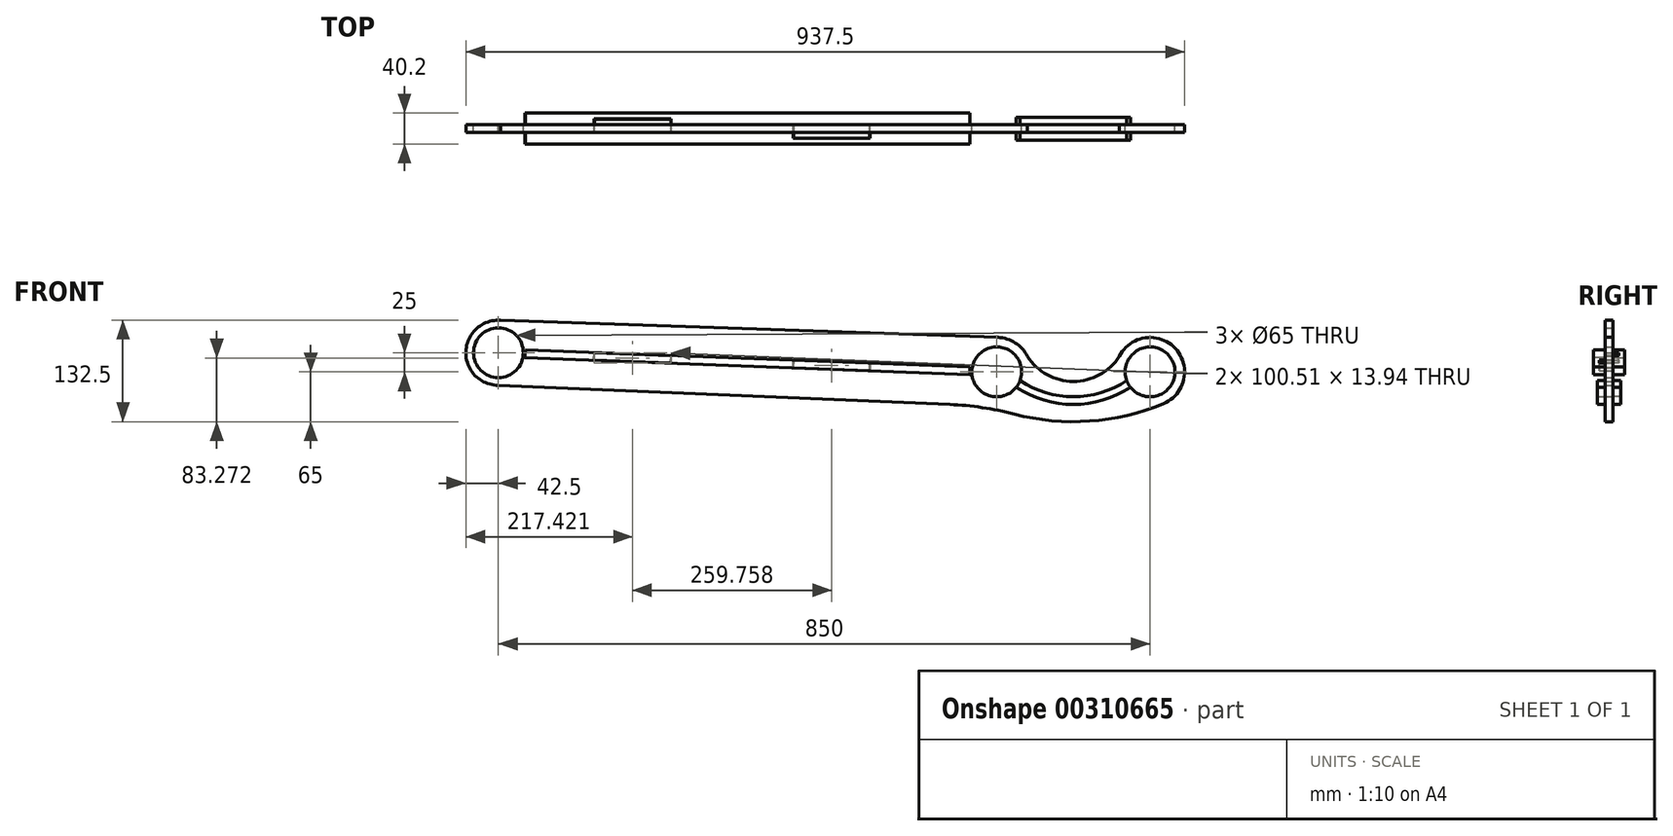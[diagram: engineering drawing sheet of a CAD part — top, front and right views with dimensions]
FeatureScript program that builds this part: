
annotation { "Feature Type Name" : "Feature", "Feature Type Description" : "" }
export const myFeature = defineFeature(function(context is Context, id is Id, definition is map)
    precondition{}
    {
        {
            var Q0;
            Q0=qCreatedBy(makeId("Front.planeOp"),FACE);
            var sketch = newSketch(context, id + "F0", { "sketchPlane" : qUnion([Q0])});
            skCircle(sketch, "E0", {"center": v(0, 0) * mm, "radius": 32.5 * mm});
            skCircle(sketch, "E1", {"center": v(0, 0) * mm, "radius": 42.5 * mm});
            skCircle(sketch, "E2", {"center": v(750, 0) * mm, "radius": 35 * mm, "construction": true});
            skArc(sketch, "E3", {"start": v(690.14, -4.65) * mm, "mid": v(674.21, 12.93) * mm, "end": v(651.55, 19.97) * mm});
            skCircle(sketch, "E4", {"center": v(850, -25) * mm, "radius": 45 * mm});
            skArc(sketch, "E5", {"start": v(687.42, 0) * mm, "mid": v(750, -37.5) * mm, "end": v(812.58, 0) * mm});
            skLineSegment(sketch, "E6", {"start": v(0, 42.5) * mm, "end": v(651.55, 19.97) * mm});
            skLineSegment(sketch, "E7", {"start": v(0, -42.5) * mm, "end": v(588.64, -67.44) * mm});
            skPoint(sketch, "E8", {"position": v(750, -90) * mm});
            skArc(sketch, "E9", {"start": v(640.42, -69.63) * mm, "mid": v(754.16, -89.97) * mm, "end": v(867.3, -66.54) * mm});
            skPoint(sketch, "E10.visualSharp", {"position": v(640.42, -69.63) * mm});
            skArc(sketch, "E10.filletArc", {"start": v(672.87, -80.09) * mm, "mid": v(631.09, -71.51) * mm, "end": v(588.64, -67.44) * mm});
            skCircle(sketch, "E11", {"center": v(650, -25) * mm, "radius": 32.5 * mm});
            skCircle(sketch, "E12", {"center": v(850, -25) * mm, "radius": 32.5 * mm});
            skArc(sketch, "E13", {"start": v(0, 42.5) * mm, "mid": v(324.91, 6.25) * mm, "end": v(651.55, 19.97) * mm});
            skArc(sketch, "E14", {"start": v(640.42, -69.63) * mm, "mid": v(321.27, -31.09) * mm, "end": v(0, -42.5) * mm});
            skSolve(sketch);
        }
        {
            var Q0;
            Q0 = qSketchRegion(id + "F0", true);
            extrude(context, id + "F1", {"entities" : qUnion([Q0]), "depth" : 5 * mm, "hasSecondDirection" : true, "secondDirectionOppositeDirection" : true, "secondDirectionDepth" : 5 * mm});
        }
        {
            var Q0;
            Q0=makeQuery(id+"F1.opExtrude","CAP_FACE",FACE,{"disambiguationData":[OSD([sQuery(id+"F0.wireOp",EDGE,"E0"),sQuery(id+"F0.wireOp",EDGE,"E1"),sQuery(id+"F0.wireOp",EDGE,"E3"),sQuery(id+"F0.wireOp",EDGE,"E4"),sQuery(id+"F0.wireOp",EDGE,"E5"),sQuery(id+"F0.wireOp",EDGE,"E6"),sQuery(id+"F0.wireOp",EDGE,"E7"),sQuery(id+"F0.wireOp",EDGE,"E9"),sQuery(id+"F0.wireOp",EDGE,"E10.filletArc"),sQuery(id+"F0.wireOp",EDGE,"E11"),sQuery(id+"F0.wireOp",EDGE,"E12")])],"isStart":true});
            var sketch = newSketch(context, id + "F2", { "sketchPlane" : qUnion([Q0])});
            skLineSegment(sketch, "E15", {"start": v(0, 0) * mm, "end": v(-650, -25) * mm, "construction": true});
            skLineSegment(sketch, "E16.bottom", {"start": v(-484.55, -23.7) * mm, "end": v(-384.42, -19.84) * mm});
            skLineSegment(sketch, "E16.top", {"start": v(-484.94, -13.6) * mm, "end": v(-384.8, -9.75) * mm});
            skLineSegment(sketch, "E16.left", {"start": v(-484.55, -23.7) * mm, "end": v(-484.94, -13.6) * mm});
            skLineSegment(sketch, "E16.right", {"start": v(-384.42, -19.84) * mm, "end": v(-384.8, -9.75) * mm});
            skLineSegment(sketch, "E17.bottom", {"start": v(-225.18, -3.6) * mm, "end": v(-125.05, 0.24) * mm});
            skLineSegment(sketch, "E17.top", {"start": v(-224.79, -13.7) * mm, "end": v(-124.66, -9.85) * mm});
            skLineSegment(sketch, "E17.left", {"start": v(-225.18, -3.6) * mm, "end": v(-224.79, -13.7) * mm});
            skLineSegment(sketch, "E17.right", {"start": v(-125.05, 0.24) * mm, "end": v(-124.66, -9.85) * mm});
            skSolve(sketch);
        }
        {
            var Q0;
            Q0=sQuery(id+"F2.wireOp",VERTEX,"E15.end");
            var Q1;
            Q1=sQuery(id+"F2.wireOp",VERTEX,"E15.start");
            var Q2;
            Q2=qCreatedBy(makeId("Origin.pointOp"),VERTEX);
            cPlane(context, id + "F3", {"entities" : qUnion([Q0, Q1, Q2]), "cplaneType" : CPlaneType.THREE_POINT, "offset" : 25 * mm, "width" : 150 * mm, "height" : 150 * mm});
        }
        {
            var Q0;
            Q0=qCreatedBy(id+"F3.planeOp",FACE);
            var sketch = newSketch(context, id + "F4", { "sketchPlane" : qUnion([Q0])});
            skLineSegment(sketch, "E18", {"start": v(35, 5.1) * mm, "end": v(35, 20.1) * mm});
            skLineSegment(sketch, "E19", {"start": v(35, 20.1) * mm, "end": v(615.5, 20.1) * mm});
            skLineSegment(sketch, "E20", {"start": v(615.5, 20.1) * mm, "end": v(615.5, 5.1) * mm});
            skLineSegment(sketch, "E21", {"start": v(615.5, 5.1) * mm, "end": v(484.7, 5.1) * mm});
            skLineSegment(sketch, "E22", {"start": v(125, 5.1) * mm, "end": v(125, -12.4) * mm});
            skLineSegment(sketch, "E23", {"start": v(125, -12.4) * mm, "end": v(225, -12.4) * mm});
            skLineSegment(sketch, "E24", {"start": v(225, -12.4) * mm, "end": v(225, 5.1) * mm});
            skLineSegment(sketch, "E25.trimOffspring", {"start": v(125, 5.1) * mm, "end": v(35, 5.1) * mm});
            skLineSegment(sketch, "E26", {"start": v(384.7, 5.1) * mm, "end": v(384.7, 12.7) * mm});
            skLineSegment(sketch, "E27", {"start": v(384.7, 12.7) * mm, "end": v(484.7, 12.7) * mm});
            skLineSegment(sketch, "E28", {"start": v(484.7, 12.7) * mm, "end": v(484.7, 5.1) * mm});
            skLineSegment(sketch, "E29.trimOffspring", {"start": v(384.7, 5.1) * mm, "end": v(225, 5.1) * mm});
            skLineSegment(sketch, "E30", {"start": v(35, -5.1) * mm, "end": v(35, -20.1) * mm});
            skLineSegment(sketch, "E31", {"start": v(35, -20.1) * mm, "end": v(615.5, -20.1) * mm});
            skLineSegment(sketch, "E32", {"start": v(615.5, -20.1) * mm, "end": v(615.5, -5.1) * mm});
            skLineSegment(sketch, "E33", {"start": v(615.5, -5.1) * mm, "end": v(225.3, -5.1) * mm});
            skLineSegment(sketch, "E34.trimOffspring", {"start": v(124.7, -5.1) * mm, "end": v(35, -5.1) * mm});
            skLineSegment(sketch, "E35", {"start": v(124.7, -5.1) * mm, "end": v(124.7, -12.7) * mm});
            skLineSegment(sketch, "E36", {"start": v(124.7, -12.7) * mm, "end": v(225.3, -12.7) * mm});
            skLineSegment(sketch, "E37", {"start": v(225.3, -12.7) * mm, "end": v(225.3, -5.1) * mm});
            skPoint(sketch, "E38.orphan", {"position": v(125, -5.1) * mm});
            skLineSegment(sketch, "E39", {"start": v(385, -5.1) * mm, "end": v(385, 12.4) * mm});
            skLineSegment(sketch, "E40", {"start": v(385, 12.4) * mm, "end": v(484.4, 12.4) * mm});
            skLineSegment(sketch, "E41", {"start": v(484.4, 12.4) * mm, "end": v(484.4, -5.1) * mm});
            skSolve(sketch);
        }
        {
            var Q0;
            Q0 = qSketchRegion(id + "F2", true);
            extrude(context, id + "F5", {"entities" : qUnion([Q0]), "operationType" : NewBodyOperationType.REMOVE, "oppositeDirection" : true, "depth" : 25 * mm});
        }
        {
            var Q0;
            Q0 = qSketchRegion(id + "F4", true);
            extrude(context, id + "F6", {"entities" : qUnion([Q0]), "depth" : 5 * mm, "hasSecondDirection" : true, "secondDirectionOppositeDirection" : true, "secondDirectionDepth" : 5 * mm});
        }
        {
            var Q0;
            Q0=makeQuery(id+"F1.opExtrude","CAP_FACE",FACE,{"disambiguationData":[OSD([sQuery(id+"F0.wireOp",EDGE,"E0"),sQuery(id+"F0.wireOp",EDGE,"E1"),sQuery(id+"F0.wireOp",EDGE,"E3"),sQuery(id+"F0.wireOp",EDGE,"E4"),sQuery(id+"F0.wireOp",EDGE,"E5"),sQuery(id+"F0.wireOp",EDGE,"E6"),sQuery(id+"F0.wireOp",EDGE,"E7"),sQuery(id+"F0.wireOp",EDGE,"E9"),sQuery(id+"F0.wireOp",EDGE,"E10.filletArc"),sQuery(id+"F0.wireOp",EDGE,"E11"),sQuery(id+"F0.wireOp",EDGE,"E12")])],"isStart":false});
            var sketch = newSketch(context, id + "F7", { "sketchPlane" : qUnion([Q0])});
            skArc(sketch, "E42", {"start": v(680.45, -36.36) * mm, "mid": v(750, -57.5) * mm, "end": v(819.55, -36.36) * mm});
            skArc(sketch, "E43.0", {"start": v(675.53, -45.1) * mm, "mid": v(750, -67.5) * mm, "end": v(824.47, -45.1) * mm});
            skArc(sketch, "E44", {"start": v(675.53, -45.1) * mm, "mid": v(678.33, -40.93) * mm, "end": v(680.45, -36.36) * mm});
            skArc(sketch, "E45", {"start": v(819.55, -36.36) * mm, "mid": v(821.67, -40.93) * mm, "end": v(824.47, -45.1) * mm});
            skSolve(sketch);
        }
        {
            var Q0;
            Q0 = qSketchRegion(id + "F7", true);
            extrude(context, id + "F8", {"entities" : qUnion([Q0]), "depth" : 10 * mm});
        }
        {
            var Q0;
            Q0=makeQuery(id+"F8.opExtrude","SWEPT_BODY",BODY,{"disambiguationData":[OSD([sQuery(id+"F7.wireOp",EDGE,"E42"),sQuery(id+"F7.wireOp",EDGE,"E43.0"),sQuery(id+"F7.wireOp",EDGE,"E44"),sQuery(id+"F7.wireOp",EDGE,"E45")])]});
            var Q1;
            Q1=qCreatedBy(makeId("Front.planeOp"),FACE);
            mirror(context, id + "F9", {"entities" : qUnion([Q0]), "mirrorPlane" : qUnion([Q1])});
        }
    });
